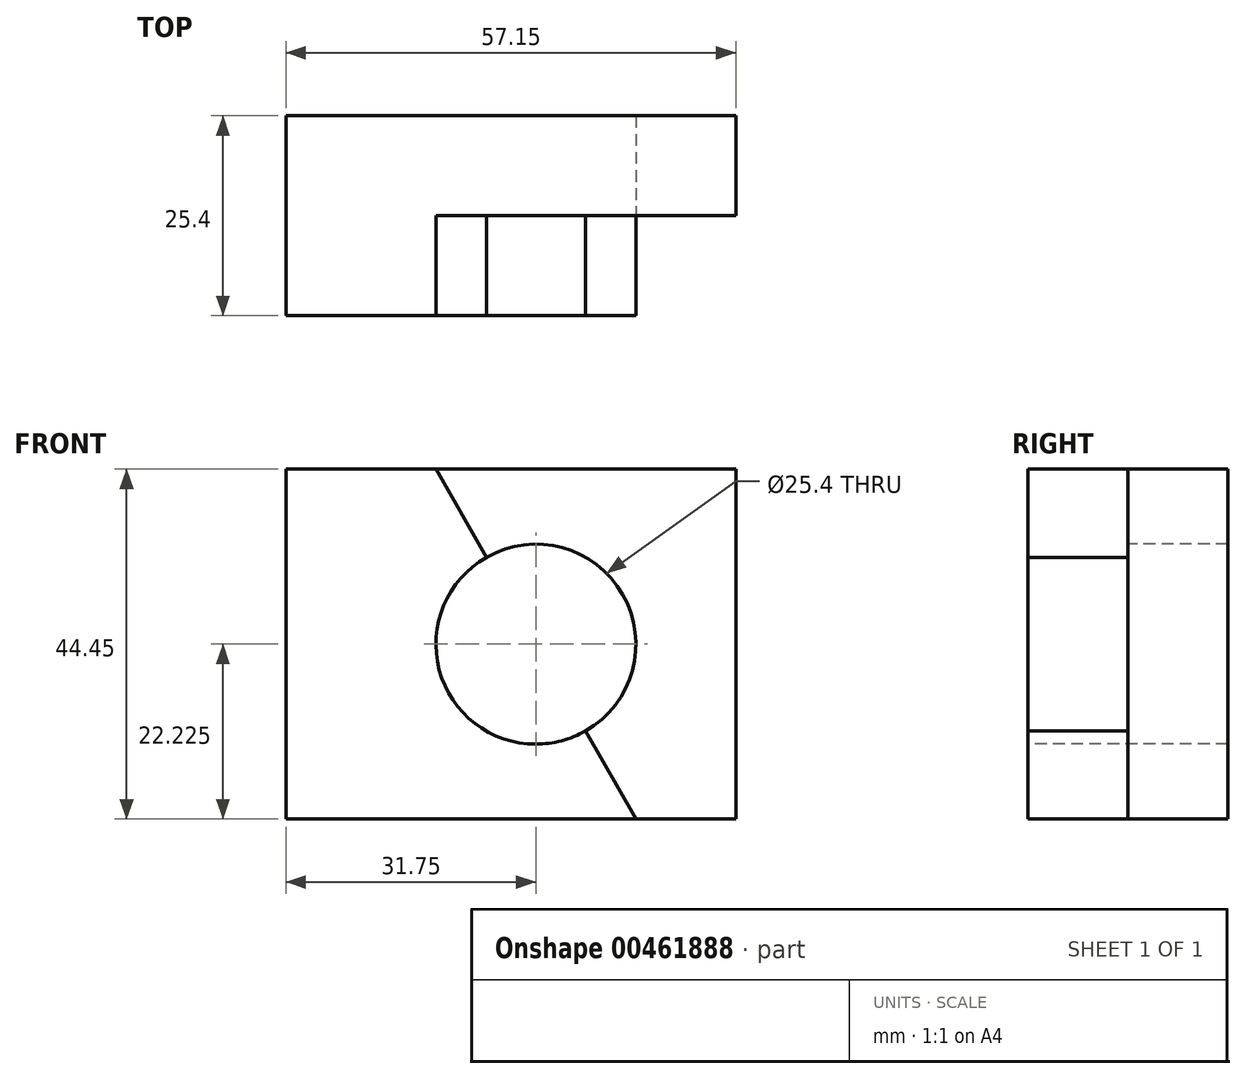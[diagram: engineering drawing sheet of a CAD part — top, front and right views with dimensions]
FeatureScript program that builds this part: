
annotation { "Feature Type Name" : "Feature", "Feature Type Description" : "" }
export const myFeature = defineFeature(function(context is Context, id is Id, definition is map)
    precondition{}
    {
        {
            var Q0;
            Q0=qCreatedBy(makeId("Right.planeOp"),FACE);
            var sketch = newSketch(context, id + "F0", { "sketchPlane" : qUnion([Q0])});
            skLineSegment(sketch, "E0.bottom", {"start": v(0, 0) * mm, "end": v(25.4, 0) * mm});
            skLineSegment(sketch, "E0.top", {"start": v(0, 44.45) * mm, "end": v(25.4, 44.45) * mm});
            skLineSegment(sketch, "E0.left", {"start": v(0, 0) * mm, "end": v(0, 44.45) * mm});
            skLineSegment(sketch, "E0.right", {"start": v(25.4, 0) * mm, "end": v(25.4, 44.45) * mm});
            skSolve(sketch);
        }
        {
            var Q0;
            Q0=makeQuery(id+"F0.imprint","IMPRINT",FACE,{"disambiguationData":[TD([[makeQuery(id+"F0.imprint","IMPRINT",EDGE,{"derivedFrom":sQuery(id+"F0.wireOp",EDGE,"E0.bottom")}),1.0]])]});
            extrude(context, id + "F1", {"entities" : qUnion([Q0]), "depth" : 57.15 * mm});
        }
        {
            var Q0;
            Q0=makeQuery(id+"F1.opExtrude","SWEPT_FACE",FACE,{"disambiguationData":[OSD([sQuery(id+"F0.wireOp",EDGE,"E0.left")])]});
            var sketch = newSketch(context, id + "F2", { "sketchPlane" : qUnion([Q0])});
            skLineSegment(sketch, "E1", {"start": v(0, 44.45) * mm, "end": v(19.05, 44.45) * mm});
            skLineSegment(sketch, "E2", {"start": v(19.05, 44.45) * mm, "end": v(44.45, 0) * mm});
            skLineSegment(sketch, "E3", {"start": v(44.45, 0) * mm, "end": v(57.15, 0) * mm});
            skSolve(sketch);
        }
        {
            var Q0;
            {var subQ0=sQuery(id+"F2.wireOp",EDGE,"E2");Q0=makeQuery(id+"F2.imprint","IMPRINT",FACE,{"disambiguationData":[TD([[makeQuery(id+"F2.imprint","IMPRINT",EDGE,{"derivedFrom":subQ0}),1.0]])]});}
            extrude(context, id + "F3", {"entities" : qUnion([Q0]), "operationType" : NewBodyOperationType.REMOVE, "oppositeDirection" : true, "depth" : 12.7 * mm});
        }
        {
            var Q0;
            Q0=makeQuery(id+"F1.opExtrude","SWEPT_FACE",FACE,{"disambiguationData":[OSD([sQuery(id+"F0.wireOp",EDGE,"E0.left")])]});
            var sketch = newSketch(context, id + "F4", { "sketchPlane" : qUnion([Q0])});
            skCircle(sketch, "E4", {"center": v(31.75, 22.22) * mm, "radius": 12.7 * mm});
            skSolve(sketch);
        }
        {
            var Q0;
            {var subQ0=sQuery(id+"F4.wireOp",EDGE,"E4");var subQ1=makeQuery(id+"F3.boolean.opBoolean","COPY",EDGE,{"derivedFrom":makeQuery(id+"F3.opExtrude","CAP_EDGE",EDGE,{"disambiguationData":[OSD([sQuery(id+"F2.wireOp",EDGE,"E2")])],"isStart":true})});var subQ2=makeQuery(id+"F4.imprint","INTERSECT",VERTEX,{"disambiguationData":[OD(0.0)],"derivedFrom":[subQ1,subQ0]});Q0=makeQuery(id+"F4.imprint","IMPRINT",FACE,{"disambiguationData":[TD([[makeQuery(id+"F4.imprint","IMPRINT",EDGE,{"disambiguationData":[TD([[subQ2,1.0]])],"derivedFrom":subQ0}),1.0]])]});}
            var Q1;
            {var subQ0=sQuery(id+"F4.wireOp",EDGE,"E4");var subQ1=makeQuery(id+"F3.boolean.opBoolean","COPY",EDGE,{"derivedFrom":makeQuery(id+"F3.opExtrude","CAP_EDGE",EDGE,{"disambiguationData":[OSD([sQuery(id+"F2.wireOp",EDGE,"E2")])],"isStart":true})});var subQ2=makeQuery(id+"F4.imprint","INTERSECT",VERTEX,{"disambiguationData":[OD(0.0)],"derivedFrom":[subQ1,subQ0]});Q1=makeQuery(id+"F4.imprint","IMPRINT",FACE,{"disambiguationData":[TD([[makeQuery(id+"F4.imprint","IMPRINT",EDGE,{"disambiguationData":[TD([[subQ2,-1.0]])],"derivedFrom":subQ0}),1.0]])]});}
            extrude(context, id + "F5", {"entities" : qUnion([Q0, Q1]), "operationType" : NewBodyOperationType.REMOVE, "oppositeDirection" : true, "depth" : 25.4 * mm});
        }
    });
